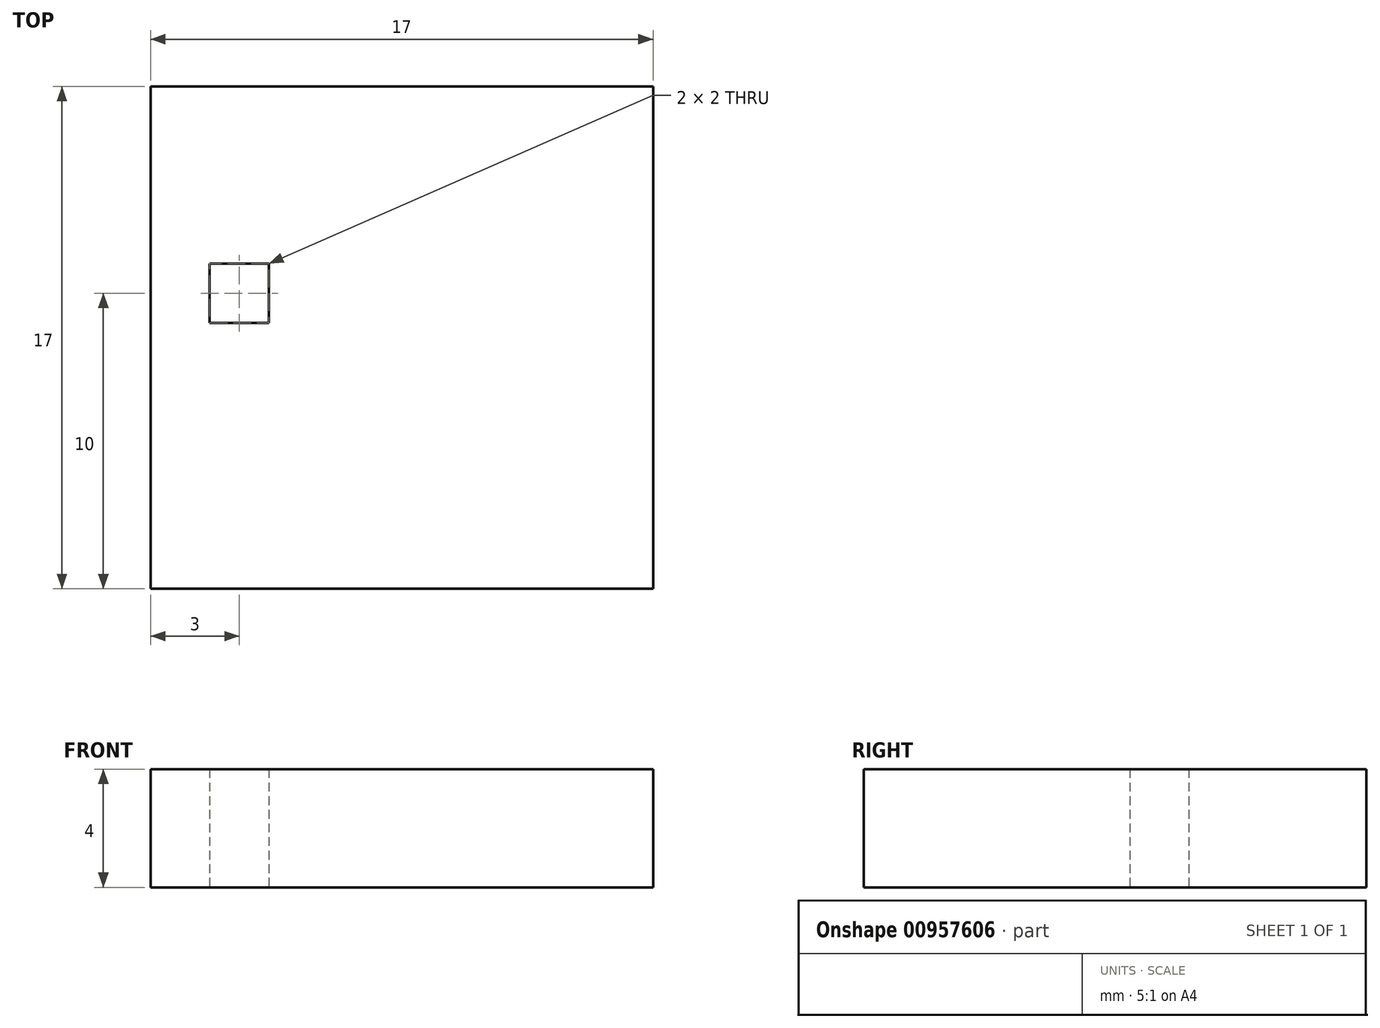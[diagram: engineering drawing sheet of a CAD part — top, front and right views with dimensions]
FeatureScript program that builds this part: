
annotation { "Feature Type Name" : "Feature", "Feature Type Description" : "" }
export const myFeature = defineFeature(function(context is Context, id is Id, definition is map)
    precondition{}
    {
        {
            var Q0;
            Q0=qCreatedBy(makeId("Top.planeOp"),FACE);
            var sketch = newSketch(context, id + "F0", { "sketchPlane" : qUnion([Q0])});
            skLineSegment(sketch, "E0.bottom", {"start": v(-8.5, 8.5) * mm, "end": v(8.5, 8.5) * mm});
            skLineSegment(sketch, "E0.top", {"start": v(-8.5, -8.5) * mm, "end": v(8.5, -8.5) * mm});
            skLineSegment(sketch, "E0.left", {"start": v(-8.5, 8.5) * mm, "end": v(-8.5, -8.5) * mm});
            skLineSegment(sketch, "E0.right", {"start": v(8.5, 8.5) * mm, "end": v(8.5, -8.5) * mm});
            skPoint(sketch, "E0.middle", {"position": v(0, 0) * mm});
            skLineSegment(sketch, "E1.bottom", {"start": v(-4.5, 2.5) * mm, "end": v(-6.5, 2.5) * mm});
            skLineSegment(sketch, "E1.top", {"start": v(-4.5, 0.5) * mm, "end": v(-6.5, 0.5) * mm});
            skLineSegment(sketch, "E1.left", {"start": v(-4.5, 2.5) * mm, "end": v(-4.5, 0.5) * mm});
            skLineSegment(sketch, "E1.right", {"start": v(-6.5, 2.5) * mm, "end": v(-6.5, 0.5) * mm});
            skSolve(sketch);
        }
        {
            var Q0;
            Q0=makeQuery(id+"F0.imprint","IMPRINT",FACE,{"disambiguationData":[TD([[makeQuery(id+"F0.imprint","IMPRINT",EDGE,{"derivedFrom":sQuery(id+"F0.wireOp",EDGE,"E0.bottom")}),-1.0]])]});
            extrude(context, id + "F1", {"entities" : qUnion([Q0]), "depth" : 4 * mm, "offsetDistance" : 25 * mm});
        }
    });
